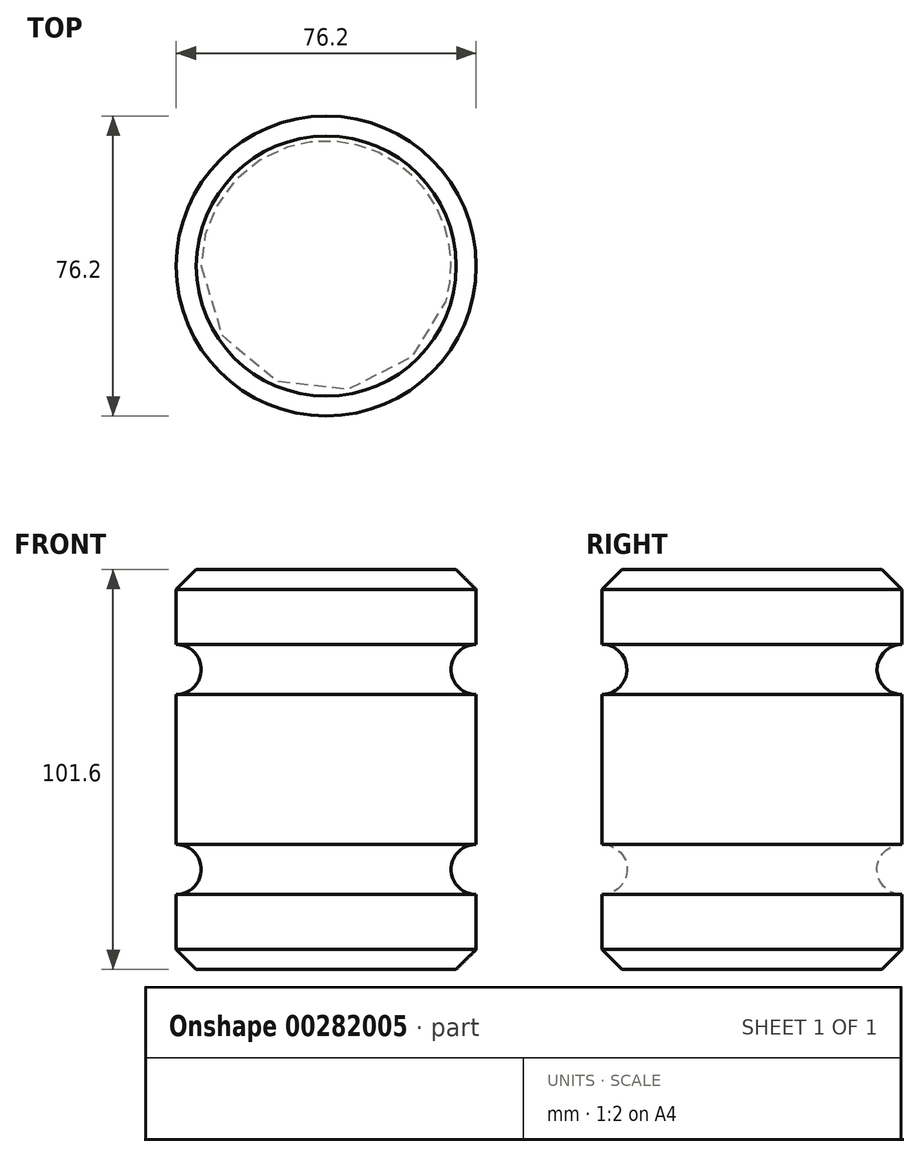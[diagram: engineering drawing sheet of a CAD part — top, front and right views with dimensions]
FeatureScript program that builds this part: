
annotation { "Feature Type Name" : "Feature", "Feature Type Description" : "" }
export const myFeature = defineFeature(function(context is Context, id is Id, definition is map)
    precondition{}
    {
        {
            var Q0;
            Q0=qCreatedBy(makeId("Front.planeOp"),FACE);
            var sketch = newSketch(context, id + "F0", { "sketchPlane" : qUnion([Q0])});
            skLineSegment(sketch, "E0.bottom", {"start": v(-0.51, 0) * mm, "end": v(-38.61, 0) * mm});
            skLineSegment(sketch, "E0.top", {"start": v(-0.51, 101.6) * mm, "end": v(-38.61, 101.6) * mm});
            skLineSegment(sketch, "E0.left", {"start": v(-0.51, 0) * mm, "end": v(-0.51, 19.05) * mm});
            skLineSegment(sketch, "E0.right", {"start": v(-38.61, 0) * mm, "end": v(-38.61, 101.6) * mm});
            skArc(sketch, "E1", {"start": v(-0.51, 82.55) * mm, "mid": v(-6.86, 76.2) * mm, "end": v(-0.51, 69.85) * mm});
            skArc(sketch, "E2", {"start": v(-0.51, 31.75) * mm, "mid": v(-6.86, 25.4) * mm, "end": v(-0.51, 19.05) * mm});
            skLineSegment(sketch, "E3.trimOffspring", {"start": v(-0.51, 31.75) * mm, "end": v(-0.51, 69.85) * mm});
            skLineSegment(sketch, "E4.trimOffspring", {"start": v(-0.51, 82.55) * mm, "end": v(-0.51, 101.6) * mm});
            skSolve(sketch);
        }
        {
            var Q0;
            Q0 = qSketchRegion(id + "F0", true);
            var Q1;
            Q1=sQuery(id+"F0.wireOp",EDGE,"E0.right");
            revolve(context, id + "F1", {"entities" : qUnion([Q0]), "axis" : qUnion([Q1]), "revolveType" : RevolveType.FULL});
        }
        {
            var Q0;
            Q0=makeQuery(id+"F1.opRevolve","SWEPT_EDGE",EDGE,{"disambiguationData":[OSD([sQuery(id+"F0.wireOp",EDGE,"E0.top"),sQuery(id+"F0.wireOp",EDGE,"E4.trimOffspring")])]});
            chamfer(context, id + "F2", {"entities" : qUnion([Q0]), "width" : 5.08 * mm, "tangentPropagation" : true});
        }
        {
            var Q0;
            Q0=makeQuery(id+"F1.opRevolve","SWEPT_FACE",FACE,{"disambiguationData":[OSD([sQuery(id+"F0.wireOp",EDGE,"E0.bottom")])]});
            chamfer(context, id + "F3", {"entities" : qUnion([Q0]), "width" : 5.08 * mm, "tangentPropagation" : true});
        }
    });
